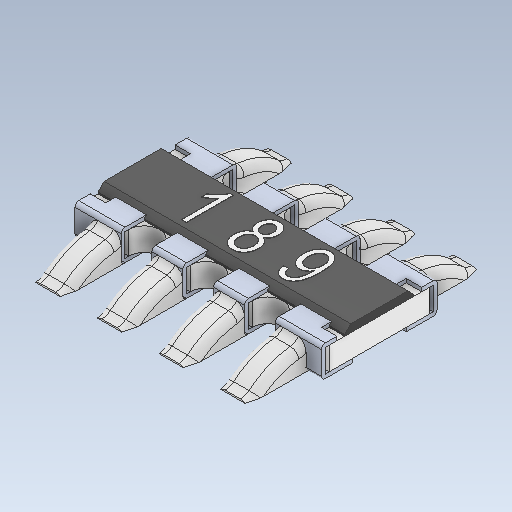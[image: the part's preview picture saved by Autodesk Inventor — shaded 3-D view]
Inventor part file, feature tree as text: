
AUTODESK INVENTOR PART (.ipt)
format: ipt  version: 2020 (Build 240168000, 168)  size: 613,888 bytes
history: native  units: in
note: dims shown in document units (in); Inventor stores cm internally (conversion verified against a paired STEP export)
features: other x8, fillet x2
ambient origin geometry x8: Origin, YZ Plane, XZ Plane, XY Plane, X Axis, Y Axis, Z Axis, Center Point
bodies: Solid1 (feature_tree), Solid2 (feature_tree), Solid3 (feature_tree), Solid4 (feature_tree), Solid5 (feature_tree), Solid6 (feature_tree), Solid7 (feature_tree), Solid8 (feature_tree), Solid9 (feature_tree), Solid10 (feature_tree)
feature tree (10):
  other  "Cut-Extrude7"
  other  "Boss-Extrude5"
  fillet  "Fillet2"  [1 undecoded]
  fillet  "Fillet1"  [1 undecoded]
  other  "LPattern3[1]"
  other  "LPattern3[2]"
  other  "LPattern3[3]"
  other  "LPattern3[4]"
  other  "LPattern3[5]"
  other  "LPattern3[6]"
note: 2 required parameter values undecoded (feature->parameter linkage not recoverable at this tier; creation-order binding heuristic only, values carry confidence <= 0.55)
